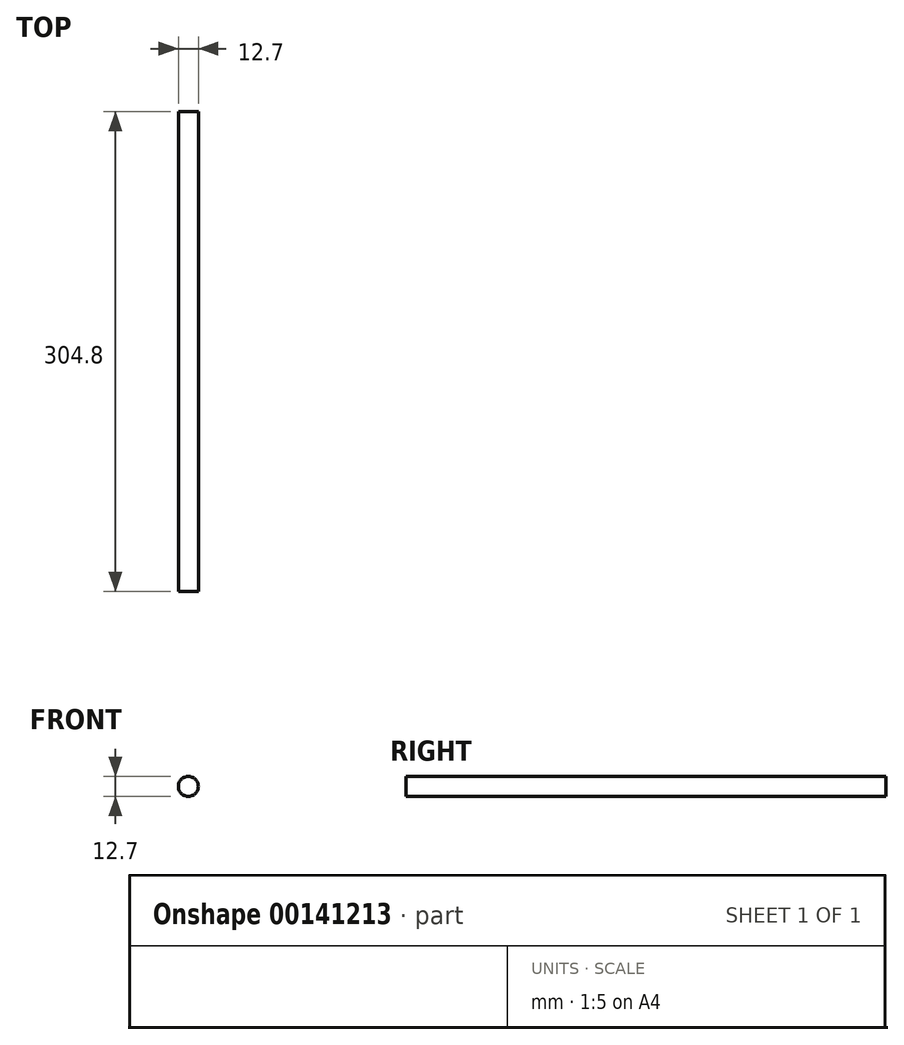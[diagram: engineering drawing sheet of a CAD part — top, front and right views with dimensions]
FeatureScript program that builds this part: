
annotation { "Feature Type Name" : "Feature", "Feature Type Description" : "" }
export const myFeature = defineFeature(function(context is Context, id is Id, definition is map)
    precondition{}
    {
        {
            var Q0;
            Q0=qCreatedBy(makeId("Front.planeOp"),FACE);
            var sketch = newSketch(context, id + "F0", { "sketchPlane" : qUnion([Q0])});
            skCircle(sketch, "E0", {"center": v(0, 0) * mm, "radius": 6.35 * mm});
            skSolve(sketch);
        }
        {
            var Q0;
            Q0=makeQuery(id+"F0.imprint","IMPRINT",FACE,{"disambiguationData":[TD([[makeQuery(id+"F0.imprint","IMPRINT",EDGE,{"derivedFrom":sQuery(id+"F0.wireOp",EDGE,"E0")}),1.0]])]});
            var Q1;
            Q1=sQuery(id+"F0.wireOp",EDGE,"E0");
            extrude(context, id + "F1", {"entities" : qUnion([Q0]), "surfaceEntities" : qUnion([Q1]), "endBound" : BoundingType.SYMMETRIC, "depth" : 304.8 * mm});
        }
    });
